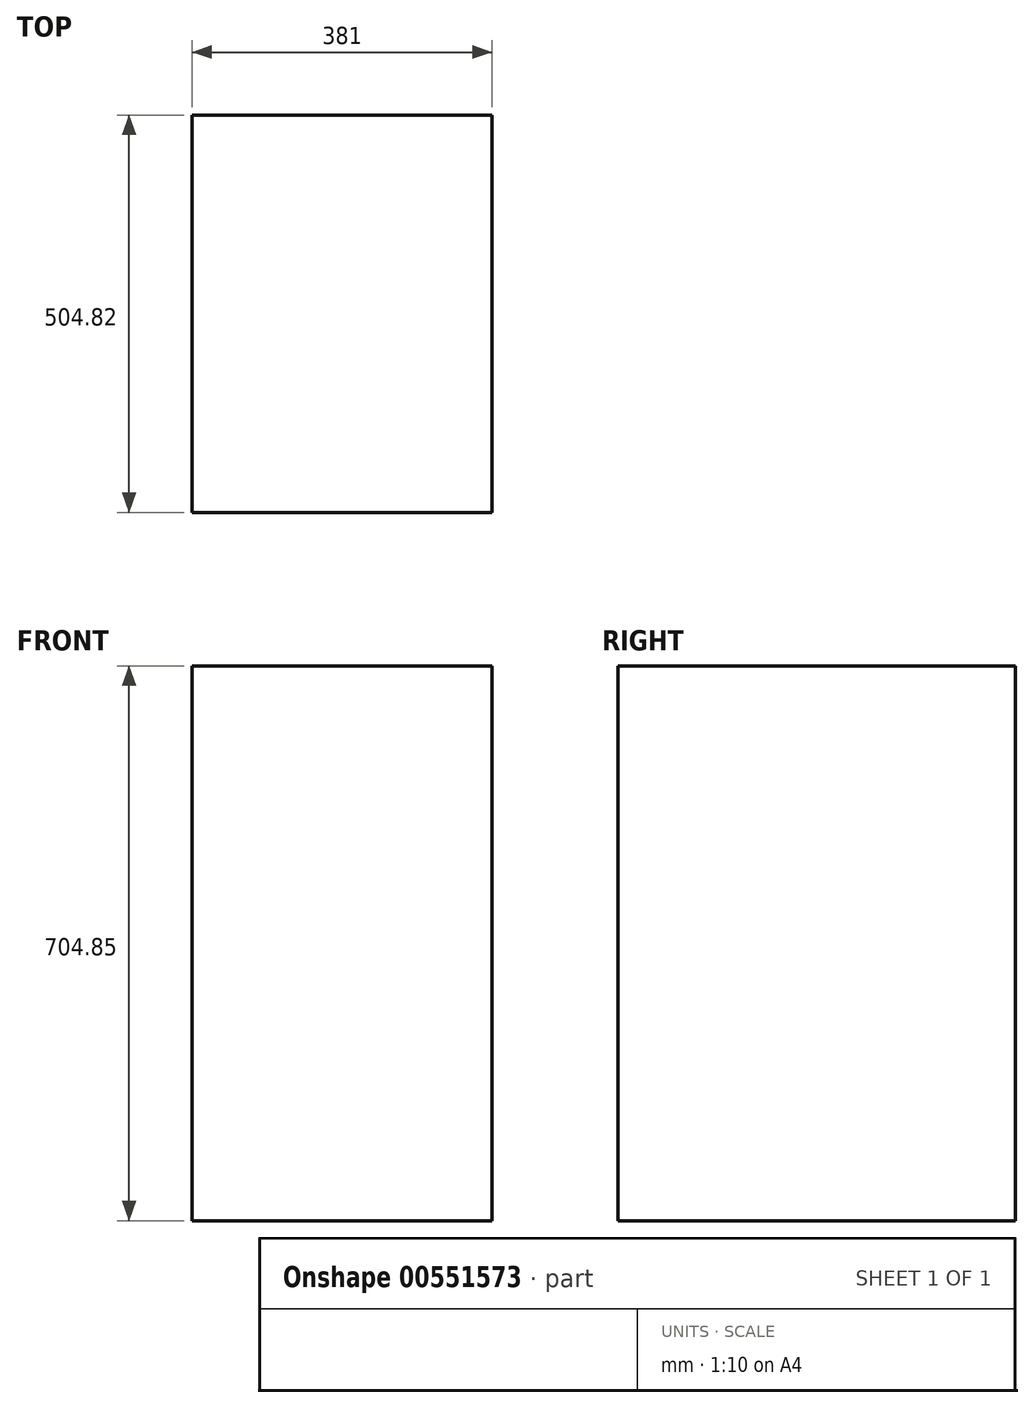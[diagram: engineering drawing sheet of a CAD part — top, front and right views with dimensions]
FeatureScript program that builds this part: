
annotation { "Feature Type Name" : "Feature", "Feature Type Description" : "" }
export const myFeature = defineFeature(function(context is Context, id is Id, definition is map)
    precondition{}
    {
        {
            var Q0;
            Q0=qCreatedBy(makeId("Top.planeOp"),FACE);
            var sketch = newSketch(context, id + "F0", { "sketchPlane" : qUnion([Q0])});
            skLineSegment(sketch, "E0.bottom", {"start": v(190.5, 252.41) * mm, "end": v(-190.5, 252.41) * mm});
            skLineSegment(sketch, "E0.top", {"start": v(190.5, -252.41) * mm, "end": v(-190.5, -252.41) * mm});
            skLineSegment(sketch, "E0.left", {"start": v(190.5, 252.41) * mm, "end": v(190.5, -252.41) * mm});
            skLineSegment(sketch, "E0.right", {"start": v(-190.5, 252.41) * mm, "end": v(-190.5, -252.41) * mm});
            skPoint(sketch, "E0.middle", {"position": v(0, 0) * mm});
            skSolve(sketch);
        }
        {
            var Q0;
            Q0=makeQuery(id+"F0.imprint","IMPRINT",FACE,{"disambiguationData":[TD([[makeQuery(id+"F0.imprint","IMPRINT",EDGE,{"derivedFrom":sQuery(id+"F0.wireOp",EDGE,"E0.bottom")}),1.0]])]});
            extrude(context, id + "F1", {"entities" : qUnion([Q0]), "depth" : 704.85 * mm, "offsetDistance" : 25.4 * mm});
        }
    });
